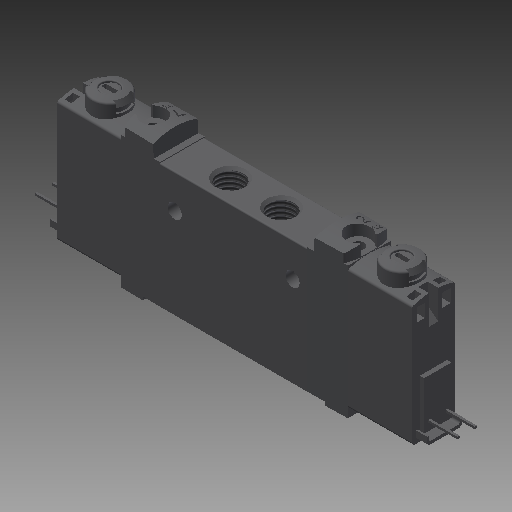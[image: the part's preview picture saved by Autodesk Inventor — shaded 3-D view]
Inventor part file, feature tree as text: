
AUTODESK INVENTOR PART (.ipt)
format: ipt  version: 2018 (Build 220112000, 112)  size: 722,432 bytes
history: native  units: mm
features: other x105, sketch x58, extrude x43, revolve x13, thread x3, hole x2
ambient origin geometry x8: Origin, YZ Plane, XZ Plane, XY Plane, X Axis, Y Axis, Z Axis, Center Point
bodies: Solid1 (feature_tree)
feature tree (224):
  extrude  "Extrusion1"  Depth=12.0mm TaperAngle=0.0deg
  extrude  "Extrusion2"  TaperAngle=360.0deg  [1 undecoded]
  extrude  "Extrusion3"  TaperAngle=360.0deg  [1 undecoded]
  sketch  "Sketch_5"  dims[d4=12.0mm d5=0.0mm d6=360.0deg]
  sketch  "Sketch_6"  dims[d7=5.4585mm d8=0.0mm d9=360.0deg]
  sketch  "Sketch_7"  dims[d10=5.4585mm d11=0.0mm d12=360.0deg d13=5.4585mm d14=0.0mm]
  revolve  "Revolution1"  Angle=360.0deg
  thread  "Thread1"  [1 undecoded]
  revolve  "Revolution2"  [1 undecoded]
  thread  "Thread2"  [1 undecoded]
  revolve  "Revolution3"  [1 undecoded]
  thread  "Thread3"  [1 undecoded]
  hole  "Hole1"  [1 undecoded]
  hole  "Hole2"  [1 undecoded]
  extrude  "Extrusion4"  Depth=4.0mm TaperAngle=0.0deg
  sketch  "Sketch_19"  dims[d43=7.7mm d44=0.0mm d45=7.7mm d46=0.0mm]
  extrude  "Extrusion5"  Depth=64.0mm TaperAngle=0.0deg
  extrude  "Extrusion6"  Depth=12.0mm TaperAngle=0.0deg
  extrude  "Extrusion7"  Depth=16.0mm TaperAngle=0.0deg
  extrude  "Extrusion8"  Depth=6.0mm TaperAngle=0.0deg
  extrude  "Extrusion9"  Depth=1.0mm TaperAngle=0.0deg
  extrude  "Extrusion10"  Depth=7.7mm TaperAngle=0.0deg
  extrude  "Extrusion11"  TaperAngle=360.0deg  [1 undecoded]
  extrude  "Extrusion12"  Depth=3.0mm TaperAngle=0.0deg
  revolve  "Revolution4"  Angle=360.0deg
  extrude  "Extrusion13"  TaperAngle=360.0deg  [1 undecoded]
  extrude  "Extrusion14"  TaperAngle=360.0deg  [1 undecoded]
  extrude  "Extrusion15"  Depth=2.15mm TaperAngle=0.0deg
  extrude  "Extrusion16"  Depth=2.1mm TaperAngle=0.0deg
  extrude  "Extrusion17"  Depth=1.5mm TaperAngle=0.0deg
  extrude  "Extrusion18"  Depth=3.0mm TaperAngle=0.0deg
  extrude  "Extrusion19"  Depth=3.0mm TaperAngle=0.0deg
  extrude  "Extrusion20"  Depth=2.0mm TaperAngle=0.0deg
  extrude  "Extrusion21"  Depth=2.0mm TaperAngle=0.0deg
  extrude  "Extrusion22"  Depth=2.0mm TaperAngle=0.0deg
  extrude  "Extrusion23"  TaperAngle=0.0deg  [1 undecoded]
  extrude  "Extrusion24"  [1 undecoded]
  extrude  "Extrusion25"  [1 undecoded]
  revolve  "Revolution5"  [1 undecoded]
  revolve  "Revolution6"  [1 undecoded]
  revolve  "Revolution7"  [1 undecoded]
  sketch  "Sketch_59"  dims[d97=1.5mm d98=0.0mm d99=3.0mm d100=0.0mm]
  sketch  "Sketch_56"  dims[d86=360.0deg d87=2.15mm d88=0.0mm]
  extrude  "Extrusion26"  [1 undecoded]
  extrude  "Extrusion27"  [1 undecoded]
  revolve  "Revolution8"  [1 undecoded]
  revolve  "Revolution9"  [1 undecoded]
  revolve  "Revolution10"  [1 undecoded]
  revolve  "Revolution11"  [1 undecoded]
  revolve  "Revolution12"  [1 undecoded]
  revolve  "Revolution13"  [1 undecoded]
  extrude  "Extrusion28"  [1 undecoded]
  extrude  "Extrusion29"  [1 undecoded]
  extrude  "Extrusion30"  [1 undecoded]
  extrude  "Extrusion31"  [1 undecoded]
  extrude  "Extrusion32"  [1 undecoded]
  extrude  "Extrusion33"  [1 undecoded]
  extrude  "Extrusion34"  [1 undecoded]
  extrude  "Extrusion35"  [1 undecoded]
  extrude  "Extrusion36"  [1 undecoded]
  extrude  "Extrusion37"  [1 undecoded]
  extrude  "Extrusion38"  [1 undecoded]
  extrude  "Extrusion39"  [1 undecoded]
  extrude  "Extrusion40"  [1 undecoded]
  extrude  "Extrusion41"  [1 undecoded]
  extrude  "Extrusion42"  [1 undecoded]
  extrude  "Extrusion43"  [1 undecoded]
  other  "DICHTUNG_XY"
  other  "DICHTUNG_YZ"
  other  "DICHTUNG_ZX"
  other  "DICHTUNG_X"
  other  "DICHTUNG_Y"
  other  "DICHTUNG_Z"
  other  "DICHTUNG_Center"
  other  "GEHAUSE_XY"
  other  "GEHAUSE_YZ"
  other  "GEHAUSE_ZX"
  other  "GEHAUSE_X"
  other  "GEHAUSE_Y"
  other  "GEHAUSE_Z"
  other  "GEHAUSE_Center"
  other  "HHB1_XY"
  other  "HHB1_YZ"
  other  "HHB1_ZX"
  other  "HHB1_X"
  other  "HHB1_Y"
  other  "HHB1_Z"
  other  "HHB1_Center"
  other  "HHB2_XY"
  other  "HHB2_YZ"
  other  "HHB2_ZX"
  other  "HHB2_X"
  other  "HHB2_Y"
  other  "HHB2_Z"
  other  "HHB2_Center"
  other  "NEBV1_XY"
  other  "NEBV1_YZ"
  other  "NEBV1_ZX"
  other  "NEBV1_X"
  other  "NEBV1_Y"
  other  "NEBV1_Z"
  other  "NEBV1_Center"
  other  "NEBV2_XY"
  other  "NEBV2_YZ"
  other  "NEBV2_ZX"
  other  "NEBV2_X"
  other  "NEBV2_Y"
  other  "NEBV2_Z"
  other  "NEBV2_Center"
  other  "QS1_XY"
  other  "QS1_YZ"
  other  "QS1_ZX"
  other  "QS1_X"
  other  "QS1_Y"
  other  "QS1_Z"
  other  "QS1_Center"
  other  "QS2_XY"
  other  "QS2_YZ"
  other  "QS2_ZX"
  other  "QS2_X"
  other  "QS2_Y"
  other  "QS2_Z"
  other  "QS2_Center"
  other  "QSZ_XY"
  other  "QSZ_YZ"
  other  "QSZ_ZX"
  other  "QSZ_X"
  other  "QSZ_Y"
  other  "QSZ_Z"
  other  "QSZ_Center"
  other  "SCREW1_XY"
  other  "SCREW1_YZ"
  other  "SCREW1_ZX"
  other  "SCREW1_X"
  other  "SCREW1_Y"
  other  "SCREW1_Z"
  other  "SCREW1_Center"
  other  "SCREW2_XY"
  other  "SCREW2_YZ"
  other  "SCREW2_ZX"
  other  "SCREW2_X"
  other  "SCREW2_Y"
  other  "SCREW2_Z"
  other  "SCREW2_Center"
  other  "U1_XY"
  other  "U1_YZ"
  other  "U1_ZX"
  other  "U1_X"
  other  "U1_Y"
  other  "U1_Z"
  other  "U1_Center"
  other  "U2_XY"
  other  "U2_YZ"
  other  "U2_ZX"
  other  "U2_X"
  other  "U2_Y"
  other  "U2_Z"
  other  "U2_Center"
  other  "VAVE1_XY"
  other  "VAVE1_YZ"
  other  "VAVE1_ZX"
  other  "VAVE1_X"
  other  "VAVE1_Y"
  other  "VAVE1_Z"
  other  "VAVE1_Center"
  other  "VAVE2_XY"
  other  "VAVE2_YZ"
  other  "VAVE2_ZX"
  other  "VAVE2_X"
  other  "VAVE2_Y"
  other  "VAVE2_Z"
  other  "VAVE2_Center"
  sketch  "Sketch_53"  dims[d84=360.0deg d85=360.0deg]
  sketch  "Sketch_143"
  sketch  "Sketch_142"
  sketch  "Sketch7"  dims[d15=5.917468mm d16=6.5415mm d17=7.0mm d18=2.0mm d19=90.0deg d20=6.8mm d21=0.0mm]
  sketch  "Sketch8"  dims[d22=5.917468mm d23=6.5415mm d24=7.0mm d25=2.0mm d26=90.0deg d27=6.8mm d28=0.0mm d29=33.1mm d30=0.0mm d31=5.0mm d32=0.0mm]
  sketch  "Sketch_17"  dims[d39=2.4mm d40=0.0mm d41=1.0mm d42=0.0mm]
  sketch  "Sketch_30"  dims[d58=5.0mm d59=0.0mm d60=16.0mm d61=0.0mm]
  sketch  "Sketch_22"  dims[d50=33.1mm d51=0.0mm d52=64.0mm d53=0.0mm]
  sketch  "Sketch_23"  dims[d54=4.0mm d55=0.0mm d56=12.0mm d57=0.0mm]
  sketch  "Sketch_120"
  sketch  "Sketch_126"
  sketch  "Sketch_123"
  sketch  "Sketch_124"
  sketch  "Sketch_125"
  sketch  "Sketch_21"  dims[d47=360.0deg d48=4.0mm d49=0.0mm]
  sketch  "Sketch_31"  dims[d62=21.34mm d63=0.0mm d64=6.0mm d65=0.0mm]
  sketch  "Sketch_32"  dims[d66=2.4mm d67=0.0mm d68=1.0mm d69=0.0mm]
  sketch  "Sketch_119"
  sketch  "Sketch_36"  dims[d76=360.0deg d77=3.0mm d78=0.0mm]
  sketch  "Sketch_37"  dims[d79=3.0mm d80=0.0mm d81=360.0deg]
  sketch  "Sketch_35"  dims[d74=360.0deg d75=360.0deg]
  sketch  "Sketch_38"  dims[d82=360.0deg d83=360.0deg]
  sketch  "Sketch_127"
  sketch  "Sketch_128"
  sketch  "Sketch_129"
  sketch  "Sketch_130"
  sketch  "Sketch_131"
  sketch  "Sketch_34"  dims[d70=7.7mm d71=0.0mm d72=7.7mm d73=0.0mm]
  sketch  "Sketch_4"  dims[d0=33.8mm d1=0.0mm d2=12.0mm d3=0.0mm]
  sketch  "Sketch_61"  dims[d105=3.0mm d106=0.0mm d107=2.0mm d108=0.0mm]
  sketch  "Sketch_57"  dims[d89=2.15mm d90=0.0mm d91=2.1mm d92=0.0mm]
  sketch  "Sketch_62"  dims[d109=2.0mm d110=0.0mm d111=2.0mm d112=0.0mm]
  sketch  "Sketch_58"  dims[d93=2.1mm d94=0.0mm d95=1.5mm d96=0.0mm]
  sketch  "Sketch_63"  dims[d113=2.0mm d114=0.0mm d115=2.0mm d116=0.0mm]
  sketch  "Sketch_64"  dims[d117=2.0mm d118=0.0mm d119=0.0mm d120=0.0mm d121=0.0mm d122=0.0mm]
  sketch  "Sketch_65"
  sketch  "Sketch_60"  dims[d101=3.0mm d102=0.0mm d103=3.0mm d104=0.0mm]
  sketch  "Sketch_66"
  sketch  "Sketch_84"
  sketch  "Sketch_81"
  sketch  "Sketch_132"
  sketch  "Sketch_133"
  sketch  "Sketch_134"
  sketch  "Sketch_135"
  sketch  "Sketch_136"
  sketch  "Sketch_137"
  sketch  "Sketch_12"  dims[d33=12.0mm d34=0.0mm d35=21.34mm d36=0.0mm d37=3.0mm d38=0.0mm]
  sketch  "Sketch_68"
  sketch  "Sketch_101"
  sketch  "Sketch_102"
  sketch  "Sketch_103"
  sketch  "Sketch_104"
note: 42 required parameter values undecoded (feature->parameter linkage not recoverable at this tier; creation-order binding heuristic only, values carry confidence <= 0.55)